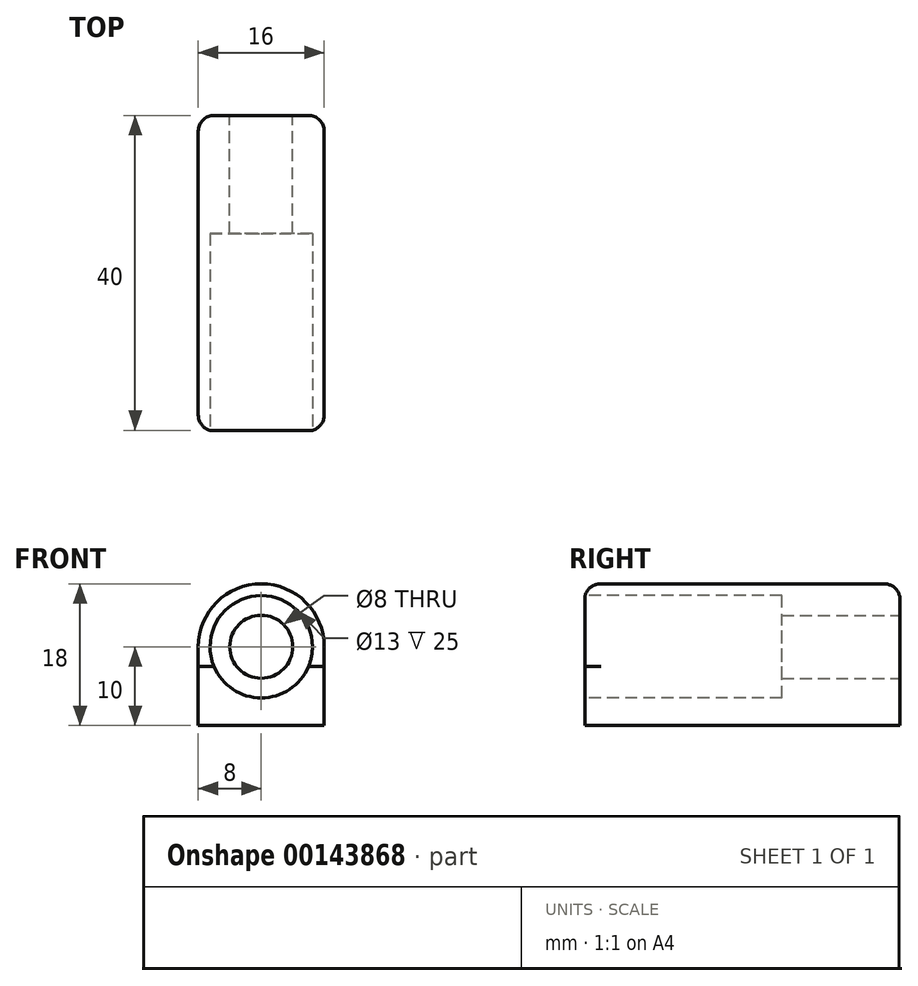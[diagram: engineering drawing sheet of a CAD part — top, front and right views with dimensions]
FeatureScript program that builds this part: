
annotation { "Feature Type Name" : "Feature", "Feature Type Description" : "" }
export const myFeature = defineFeature(function(context is Context, id is Id, definition is map)
    precondition{}
    {
        {
            var Q0;
            Q0=qCreatedBy(makeId("Front.planeOp"),FACE);
            var sketch = newSketch(context, id + "F0", { "sketchPlane" : qUnion([Q0])});
            skCircle(sketch, "E0", {"center": v(0, 0) * mm, "radius": 4 * mm});
            skCircle(sketch, "E1", {"center": v(0, 0) * mm, "radius": 8 * mm});
            skLineSegment(sketch, "E2", {"start": v(-8, 0) * mm, "end": v(-8, -10) * mm});
            skLineSegment(sketch, "E3", {"start": v(-8, -10) * mm, "end": v(8, -10) * mm});
            skLineSegment(sketch, "E4", {"start": v(8, -10) * mm, "end": v(8, 0) * mm});
            skSolve(sketch);
        }
        {
            var Q0;
            Q0=makeQuery(id+"F0.imprint","IMPRINT",FACE,{"disambiguationData":[TD([[makeQuery(id+"F0.imprint","IMPRINT",EDGE,{"derivedFrom":sQuery(id+"F0.wireOp",EDGE,"E0")}),-1.0]])]});
            var Q1;
            {var subQ0=sQuery(id+"F0.wireOp",EDGE,"E2");Q1=makeQuery(id+"F0.imprint","IMPRINT",FACE,{"disambiguationData":[TD([[makeQuery(id+"F0.imprint","IMPRINT",EDGE,{"derivedFrom":subQ0}),1.0]])]});}
            extrude(context, id + "F1", {"entities" : qUnion([Q0, Q1]), "depth" : 40 * mm, "offsetDistance" : 25 * mm});
        }
        {
            var Q0;
            Q0=makeQuery(id+"F1.opExtrude","CAP_FACE",FACE,{"disambiguationData":[OSD([sQuery(id+"F0.wireOp",EDGE,"E0"),sQuery(id+"F0.wireOp",EDGE,"E1"),sQuery(id+"F0.wireOp",EDGE,"E2"),sQuery(id+"F0.wireOp",EDGE,"E3"),sQuery(id+"F0.wireOp",EDGE,"E4")])],"isStart":false});
            var sketch = newSketch(context, id + "F2", { "sketchPlane" : qUnion([Q0])});
            skCircle(sketch, "E5", {"center": v(0, 0) * mm, "radius": 6.5 * mm});
            skSolve(sketch);
        }
        {
            var Q0;
            Q0=makeQuery(id+"F2.imprint","IMPRINT",FACE,{"disambiguationData":[TD([[makeQuery(id+"F2.imprint","IMPRINT",EDGE,{"derivedFrom":sQuery(id+"F2.wireOp",EDGE,"E5")}),1.0]])]});
            extrude(context, id + "F3", {"entities" : qUnion([Q0]), "operationType" : NewBodyOperationType.REMOVE, "oppositeDirection" : true, "depth" : 25 * mm, "offsetDistance" : 25 * mm});
        }
        {
            var Q0;
            Q0=makeQuery(id+"F1.opExtrude","CAP_EDGE",EDGE,{"disambiguationData":[OSD([sQuery(id+"F0.wireOp",EDGE,"E1")])],"isStart":false});
            var Q1;
            Q1=makeQuery(id+"F1.opExtrude","CAP_EDGE",EDGE,{"disambiguationData":[OSD([sQuery(id+"F0.wireOp",EDGE,"E1")])],"isStart":true});
            fillet(context, id + "F4", {"entities" : qUnion([Q0, Q1]), "radius" : 2 * mm, "tangentPropagation" : true, "allowEdgeOverflow" : false});
        }
    });
